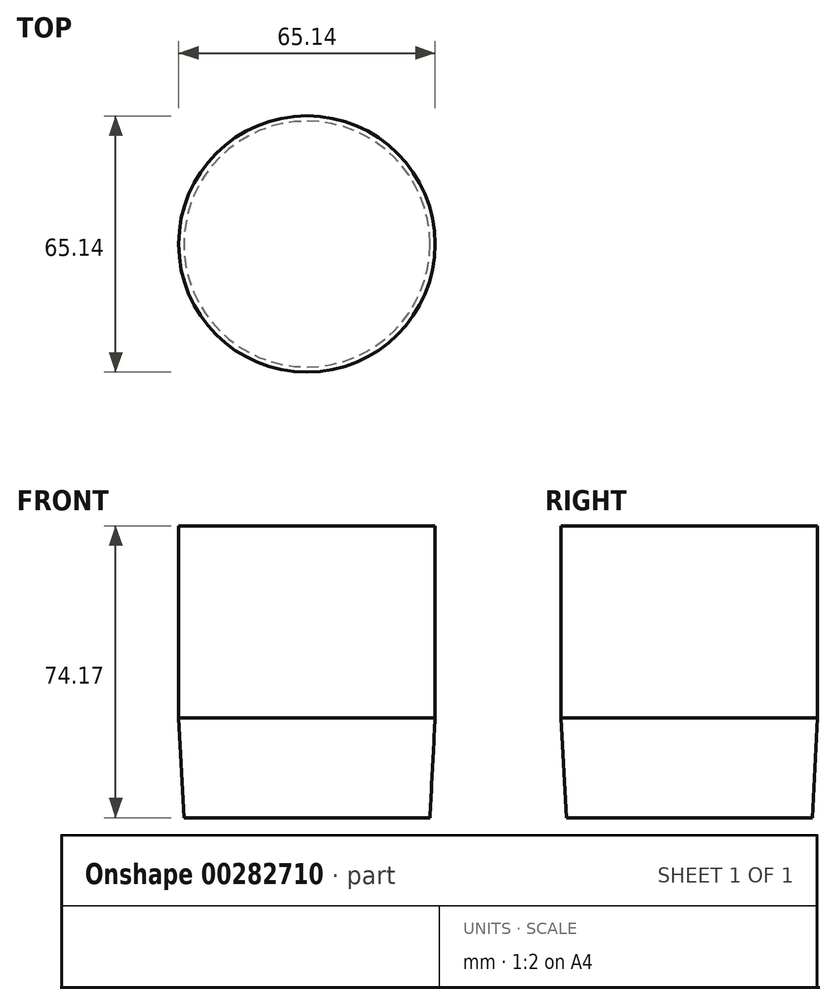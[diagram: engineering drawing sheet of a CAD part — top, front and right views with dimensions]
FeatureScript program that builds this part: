
annotation { "Feature Type Name" : "Feature", "Feature Type Description" : "" }
export const myFeature = defineFeature(function(context is Context, id is Id, definition is map)
    precondition{}
    {
        {
            var Q0;
            Q0=qCreatedBy(makeId("Top.planeOp"),FACE);
            var sketch = newSketch(context, id + "F0", { "sketchPlane" : qUnion([Q0])});
            skCircle(sketch, "E0", {"center": v(0, 0) * mm, "radius": 32.57 * mm});
            skSolve(sketch);
        }
        {
            var Q0;
            Q0 = qSketchRegion(id + "F0", true);
            extrude(context, id + "F1", {"entities" : qUnion([Q0]), "depth" : 48.77 * mm, "hasSecondDirection" : true, "secondDirectionOppositeDirection" : true, "secondDirectionDepth" : 25.4 * mm, "hasSecondDirectionDraft" : true, "secondDirectionDraftAngle" : 3 * degree, "secondDirectionDraftPullDirection" : true});
        }
    });
